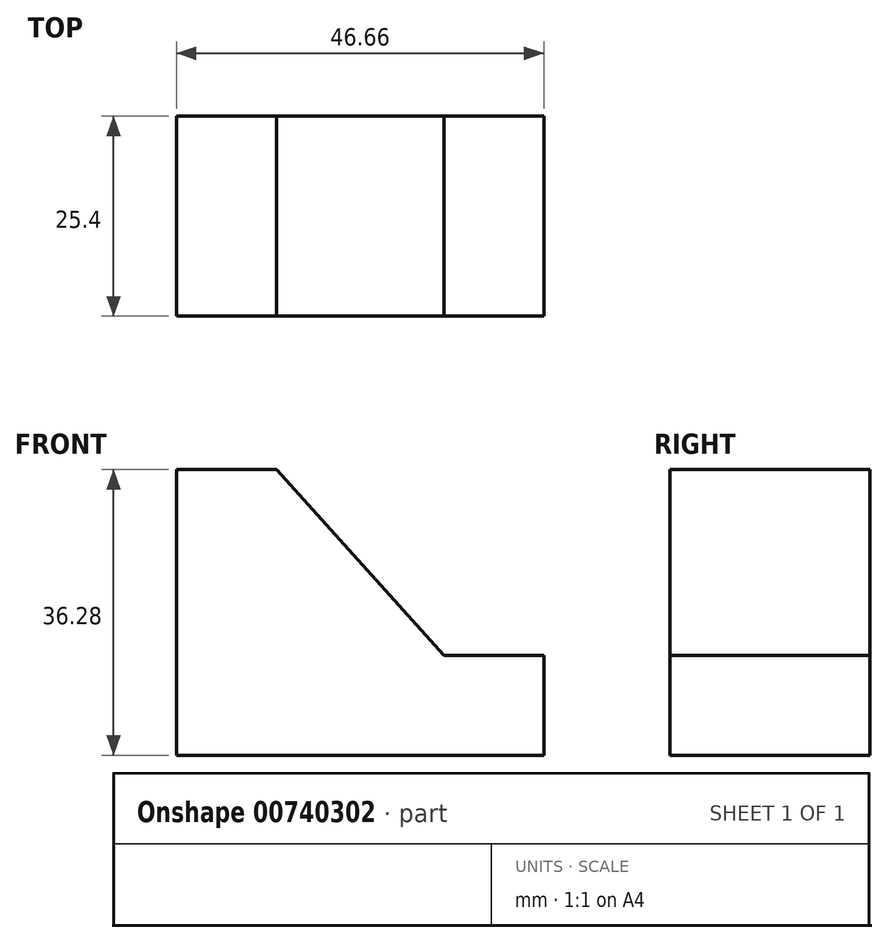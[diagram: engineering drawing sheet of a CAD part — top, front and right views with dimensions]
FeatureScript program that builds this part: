
annotation { "Feature Type Name" : "Feature", "Feature Type Description" : "" }
export const myFeature = defineFeature(function(context is Context, id is Id, definition is map)
    precondition{}
    {
        {
            var Q0;
            Q0=qCreatedBy(makeId("Front.planeOp"),FACE);
            var sketch = newSketch(context, id + "F0", { "sketchPlane" : qUnion([Q0])});
            skLineSegment(sketch, "E0", {"start": v(0, 0) * mm, "end": v(46.66, 0) * mm});
            skLineSegment(sketch, "E1", {"start": v(46.66, 0) * mm, "end": v(46.66, 12.7) * mm});
            skLineSegment(sketch, "E2", {"start": v(46.66, 12.7) * mm, "end": v(33.96, 12.7) * mm});
            skLineSegment(sketch, "E3", {"start": v(33.96, 12.7) * mm, "end": v(12.7, 36.28) * mm});
            skLineSegment(sketch, "E4", {"start": v(12.7, 36.28) * mm, "end": v(0, 36.28) * mm});
            skLineSegment(sketch, "E5", {"start": v(0, 36.28) * mm, "end": v(0, 0) * mm});
            skSolve(sketch);
        }
        {
            var Q0;
            Q0 = qSketchRegion(id + "F0", true);
            extrude(context, id + "F1", {"entities" : qUnion([Q0]), "depth" : 25.4 * mm, "offsetDistance" : 25.4 * mm});
        }
    });
